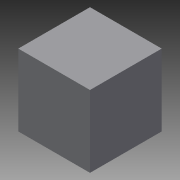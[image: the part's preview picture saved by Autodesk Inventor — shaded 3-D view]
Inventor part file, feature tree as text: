
AUTODESK INVENTOR PART (.ipt)
format: ipt  version: 2014 SP1 (Build 180222100, 222)  size: 68,096 bytes
history: native  units: mm
features: extrude x1, sketch x1
ambient origin geometry x8: Origin, YZ Plane, XZ Plane, XY Plane, X Axis, Y Axis, Z Axis, Center Point
bodies: Solid1 (feature_tree)
feature tree (2):
  extrude  "Extrusion1"  Depth=300.0mm
  sketch  "Sketch2"  dims[d0=300.0mm d1=300.0mm d2=300.0mm d3=0.0mm]
